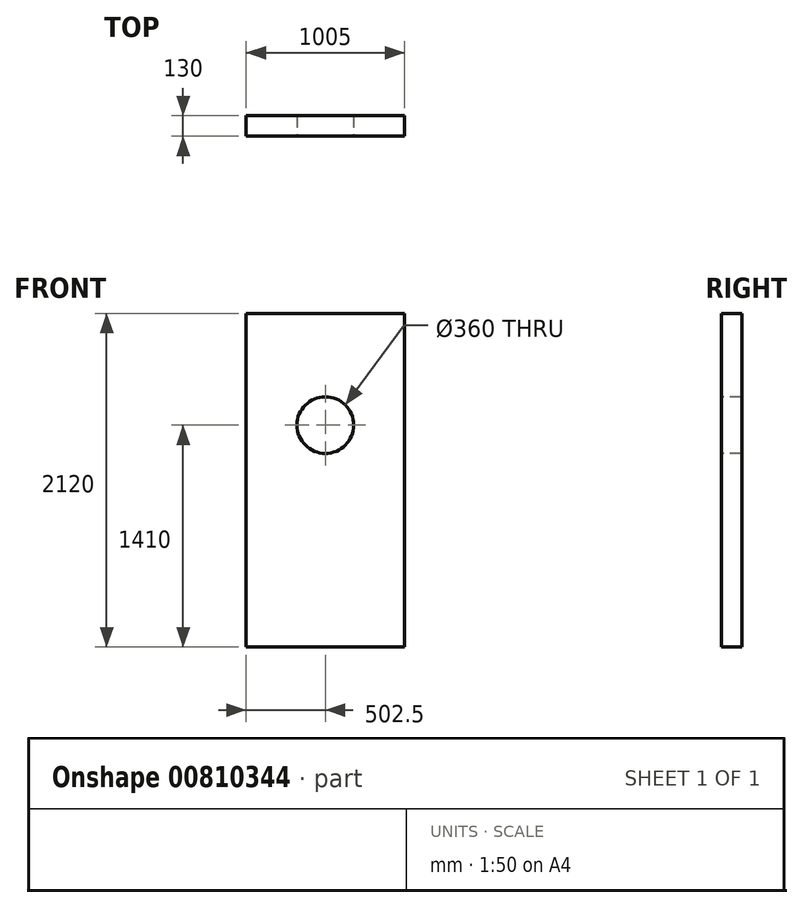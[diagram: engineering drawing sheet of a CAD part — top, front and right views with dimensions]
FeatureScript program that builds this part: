
annotation { "Feature Type Name" : "Feature", "Feature Type Description" : "" }
export const myFeature = defineFeature(function(context is Context, id is Id, definition is map)
    precondition{}
    {
        {
            var Q0;
            Q0=qCreatedBy(makeId("Top.planeOp"),FACE);
            var sketch = newSketch(context, id + "F0", { "sketchPlane" : qUnion([Q0])});
            skLineSegment(sketch, "E0.bottom", {"start": v(-502.5, 65) * mm, "end": v(502.5, 65) * mm});
            skLineSegment(sketch, "E0.top", {"start": v(-502.5, -65) * mm, "end": v(502.5, -65) * mm});
            skLineSegment(sketch, "E0.left", {"start": v(-502.5, 65) * mm, "end": v(-502.5, -65) * mm});
            skLineSegment(sketch, "E0.right", {"start": v(502.5, 65) * mm, "end": v(502.5, -65) * mm});
            skLineSegment(sketch, "E1", {"start": v(-367.7, 0) * mm, "end": v(351.49, 0) * mm, "construction": true});
            skLineSegment(sketch, "E2", {"start": v(0, 148.78) * mm, "end": v(0, -128.51) * mm, "construction": true});
            skSolve(sketch);
        }
        {
            var Q0;
            Q0 = qSketchRegion(id + "F0", true);
            extrude(context, id + "F1", {"entities" : qUnion([Q0]), "depth" : 2120 * mm, "offsetDistance" : 25.4 * mm});
        }
        {
            var Q0;
            Q0=makeQuery(id+"F1.opExtrude","SWEPT_FACE",FACE,{"disambiguationData":[OSD([sQuery(id+"F0.wireOp",EDGE,"E0.top")])]});
            var sketch = newSketch(context, id + "F2", { "sketchPlane" : qUnion([Q0])});
            skCircle(sketch, "E3", {"center": v(0, 1410) * mm, "radius": 180 * mm});
            skSolve(sketch);
        }
        {
            var Q0;
            Q0 = qSketchRegion(id + "F2", true);
            extrude(context, id + "F3", {"entities" : qUnion([Q0]), "operationType" : NewBodyOperationType.REMOVE, "endBound" : BoundingType.UP_TO_NEXT, "oppositeDirection" : true, "depth" : 25.4 * mm, "offsetDistance" : 25.4 * mm});
        }
    });
